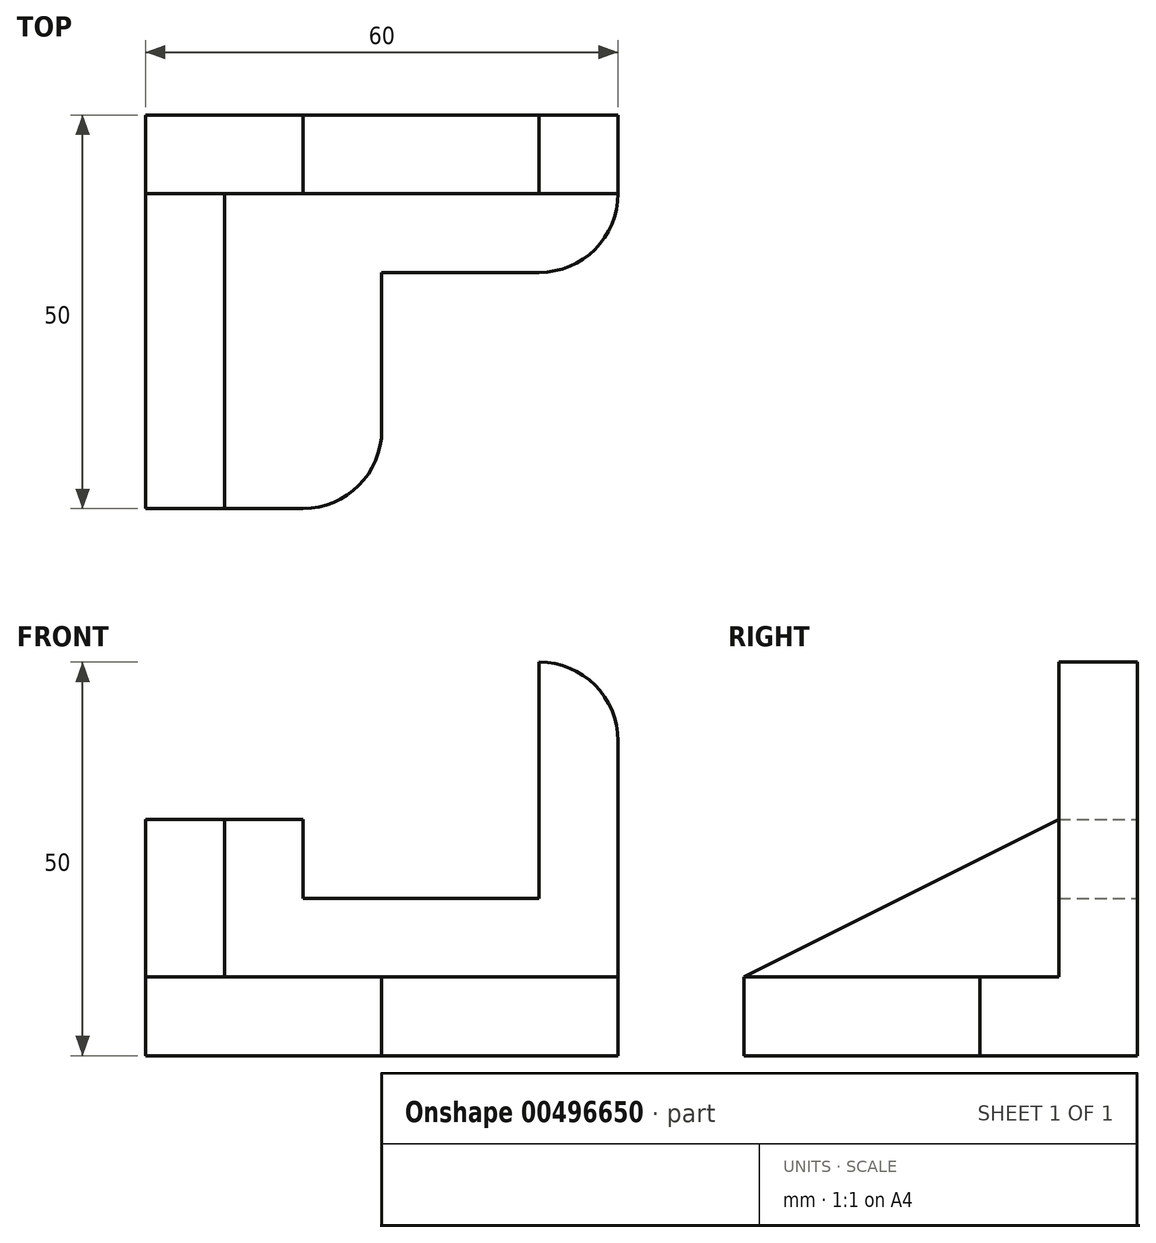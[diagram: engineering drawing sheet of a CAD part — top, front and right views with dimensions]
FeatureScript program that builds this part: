
annotation { "Feature Type Name" : "Feature", "Feature Type Description" : "" }
export const myFeature = defineFeature(function(context is Context, id is Id, definition is map)
    precondition{}
    {
        {
            var Q0;
            Q0=qCreatedBy(makeId("Top.planeOp"),FACE);
            var sketch = newSketch(context, id + "F0", { "sketchPlane" : qUnion([Q0])});
            skLineSegment(sketch, "E0", {"start": v(0, 0) * mm, "end": v(0, 50) * mm});
            skLineSegment(sketch, "E1", {"start": v(0, 50) * mm, "end": v(60, 50) * mm});
            skLineSegment(sketch, "E2", {"start": v(60, 50) * mm, "end": v(60, 40) * mm});
            skLineSegment(sketch, "E3", {"start": v(50, 30) * mm, "end": v(30, 30) * mm});
            skLineSegment(sketch, "E4", {"start": v(30, 30) * mm, "end": v(30, 10) * mm});
            skLineSegment(sketch, "E5", {"start": v(20, 0) * mm, "end": v(0, 0) * mm});
            skPoint(sketch, "E6.visualSharp", {"position": v(60, 30) * mm});
            skArc(sketch, "E6.filletArc", {"start": v(50, 30) * mm, "mid": v(57.07, 32.93) * mm, "end": v(60, 40) * mm});
            skPoint(sketch, "E7.visualSharp", {"position": v(30, 0) * mm});
            skArc(sketch, "E7.filletArc", {"start": v(20, 0) * mm, "mid": v(27.07, 2.93) * mm, "end": v(30, 10) * mm});
            skSolve(sketch);
        }
        {
            var Q0;
            Q0 = qSketchRegion(id + "F0", true);
            extrude(context, id + "F1", {"entities" : qUnion([Q0]), "depth" : 10 * mm});
        }
        {
            var Q0;
            Q0=makeQuery(id+"F1.opExtrude","SWEPT_FACE",FACE,{"disambiguationData":[OSD([sQuery(id+"F0.wireOp",EDGE,"E1")])]});
            var sketch = newSketch(context, id + "F2", { "sketchPlane" : qUnion([Q0])});
            skLineSegment(sketch, "E8", {"start": v(0, 10) * mm, "end": v(0, 30) * mm});
            skLineSegment(sketch, "E9", {"start": v(0, 30) * mm, "end": v(-20, 30) * mm});
            skLineSegment(sketch, "E10", {"start": v(-20, 30) * mm, "end": v(-20, 20) * mm});
            skLineSegment(sketch, "E11", {"start": v(-20, 20) * mm, "end": v(-50, 20) * mm});
            skLineSegment(sketch, "E12", {"start": v(-50, 20) * mm, "end": v(-50, 50) * mm});
            skLineSegment(sketch, "E13", {"start": v(-50, 50) * mm, "end": v(-50, 50) * mm});
            skLineSegment(sketch, "E14", {"start": v(-60, 40) * mm, "end": v(-60, 10) * mm});
            skPoint(sketch, "E15.visualSharp", {"position": v(-60, 50) * mm});
            skArc(sketch, "E15.filletArc", {"start": v(-50, 50) * mm, "mid": v(-57.07, 47.07) * mm, "end": v(-60, 40) * mm});
            skLineSegment(sketch, "E16", {"start": v(0, 10) * mm, "end": v(-60, 10) * mm});
            skSolve(sketch);
        }
        {
            var Q0;
            Q0 = qSketchRegion(id + "F2", true);
            extrude(context, id + "F3", {"entities" : qUnion([Q0]), "operationType" : NewBodyOperationType.ADD, "oppositeDirection" : true, "depth" : 10 * mm});
        }
        {
            var Q0;
            Q0=makeQuery(id+"F3.boolean.opBoolean","MERGE",FACE,{"derivedFrom":[makeQuery(id+"F1.opExtrude","SWEPT_FACE",FACE,{"disambiguationData":[OSD([sQuery(id+"F0.wireOp",EDGE,"E0")])]}),makeQuery(id+"F3.opExtrude","SWEPT_FACE",FACE,{"disambiguationData":[OSD([sQuery(id+"F2.wireOp",EDGE,"E8")])]})]});
            var sketch = newSketch(context, id + "F4", { "sketchPlane" : qUnion([Q0])});
            skLineSegment(sketch, "E17", {"start": v(-40, 30) * mm, "end": v(0, 10) * mm});
            skLineSegment(sketch, "E18", {"start": v(-40, 10) * mm, "end": v(0, 10) * mm});
            skLineSegment(sketch, "E19", {"start": v(-40, 30) * mm, "end": v(-40, 10) * mm});
            skSolve(sketch);
        }
        {
            var Q0;
            Q0 = qSketchRegion(id + "F4", true);
            extrude(context, id + "F5", {"entities" : qUnion([Q0]), "operationType" : NewBodyOperationType.ADD, "oppositeDirection" : true, "depth" : 10 * mm});
        }
    });
